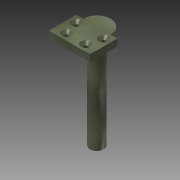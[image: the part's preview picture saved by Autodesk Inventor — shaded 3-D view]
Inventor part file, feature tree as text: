
AUTODESK INVENTOR PART (.ipt)
format: ipt  version: 2015 (Build 190159000, 159)  size: 116,736 bytes
history: native  units: mm
features: extrude x2, sketch x2, chamfer x1
ambient origin geometry x8: Origin, YZ Plane, XZ Plane, XY Plane, X Axis, Y Axis, Z Axis, Center Point
bodies: 实体1 (feature_tree)
feature tree (5):
  extrude  "拉伸1"  Depth=30.0mm
  extrude  "拉伸2"  Depth=70.0mm
  chamfer  "倒角1"  Distance=3.0mm
  sketch  "草图1"  dims[d0=20.0mm d1=30.0mm]
  sketch  "草图2"  dims[d2=20.0mm d3=3.0mm d4=3.0mm d5=3.0mm d6=3.0mm d7=5.0mm d8=5.0mm d9=5.0mm d10=5.0mm d11=8.0mm d12=5.0mm d13=5.0mm d14=8.0mm d15=5.0mm d16=0.0mm d17=10.0mm d18=70.0mm d19=0.0mm d20=2.0mm d21=2.0mm d22=45.0deg]
